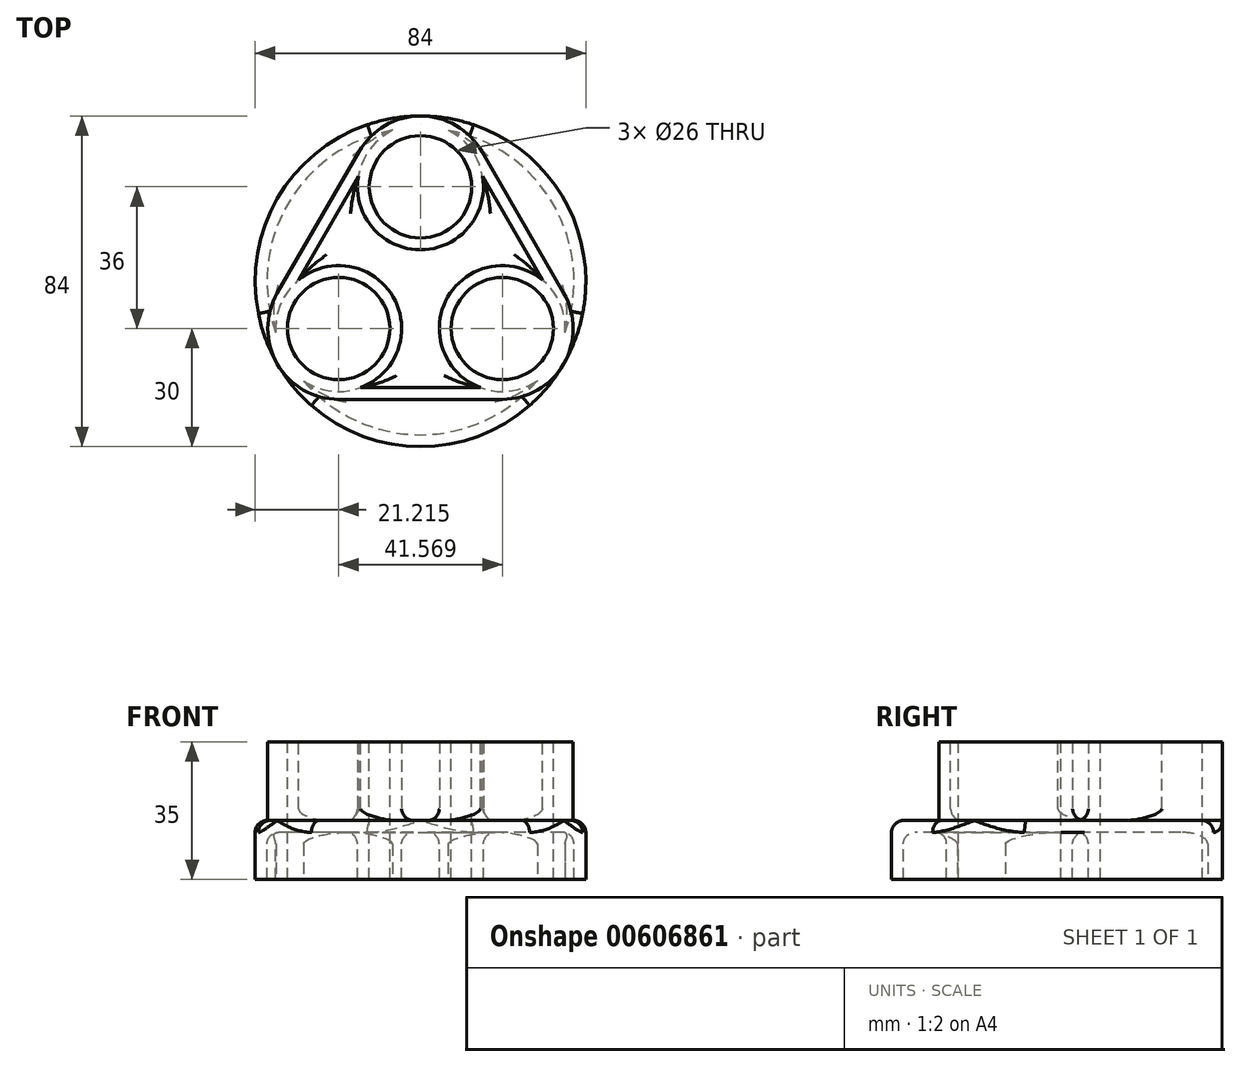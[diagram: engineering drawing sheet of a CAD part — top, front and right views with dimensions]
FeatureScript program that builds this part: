
annotation { "Feature Type Name" : "Feature", "Feature Type Description" : "" }
export const myFeature = defineFeature(function(context is Context, id is Id, definition is map)
    precondition{}
    {
        {
            var Q0;
            Q0=qCreatedBy(makeId("Top.planeOp"),FACE);
            var sketch = newSketch(context, id + "F0", { "sketchPlane" : qUnion([Q0])});
            skCircle(sketch, "E0", {"center": v(0, 24) * mm, "radius": 13 * mm});
            skLineSegment(sketch, "E1", {"start": v(0, 24) * mm, "end": v(0, 0) * mm, "construction": true});
            skCircle(sketch, "E2", {"center": v(-20.78, -12) * mm, "radius": 13 * mm});
            skCircle(sketch, "E3", {"center": v(20.78, -12) * mm, "radius": 13 * mm});
            skLineSegment(sketch, "E4", {"start": v(0, 0) * mm, "end": v(-20.78, -12) * mm, "construction": true});
            skLineSegment(sketch, "E5", {"start": v(0, 0) * mm, "end": v(20.78, -12) * mm, "construction": true});
            skCircle(sketch, "E6", {"center": v(0, 0) * mm, "radius": 42 * mm});
            skCircle(sketch, "E7.0", {"center": v(0, 24) * mm, "radius": 16 * mm});
            skCircle(sketch, "E8.0", {"center": v(-20.78, -12) * mm, "radius": 16 * mm});
            skCircle(sketch, "E9.0", {"center": v(20.78, -12) * mm, "radius": 16 * mm});
            skSolve(sketch);
        }
        {
            var Q0;
            Q0=makeQuery(id+"F0.imprint","IMPRINT",FACE,{"disambiguationData":[TD([[makeQuery(id+"F0.imprint","IMPRINT",EDGE,{"derivedFrom":sQuery(id+"F0.wireOp",EDGE,"E6")}),1.0]])]});
            var Q1;
            Q1=makeQuery(id+"F0.imprint","IMPRINT",FACE,{"disambiguationData":[TD([[makeQuery(id+"F0.imprint","IMPRINT",EDGE,{"derivedFrom":sQuery(id+"F0.wireOp",EDGE,"E3")}),-1.0]])]});
            var Q2;
            Q2=makeQuery(id+"F0.imprint","IMPRINT",FACE,{"disambiguationData":[TD([[makeQuery(id+"F0.imprint","IMPRINT",EDGE,{"derivedFrom":sQuery(id+"F0.wireOp",EDGE,"E0")}),-1.0]])]});
            var Q3;
            Q3=makeQuery(id+"F0.imprint","IMPRINT",FACE,{"disambiguationData":[TD([[makeQuery(id+"F0.imprint","IMPRINT",EDGE,{"derivedFrom":sQuery(id+"F0.wireOp",EDGE,"E2")}),-1.0]])]});
            extrude(context, id + "F1", {"entities" : qUnion([Q0, Q1, Q2, Q3]), "oppositeDirection" : true, "depth" : 15 * mm, "offsetDistance" : 25 * mm});
        }
        {
            var Q0;
            Q0=makeQuery(id+"F0.imprint","IMPRINT",FACE,{"disambiguationData":[TD([[makeQuery(id+"F0.imprint","IMPRINT",EDGE,{"derivedFrom":sQuery(id+"F0.wireOp",EDGE,"E3")}),-1.0]])]});
            var Q1;
            Q1=makeQuery(id+"F0.imprint","IMPRINT",FACE,{"disambiguationData":[TD([[makeQuery(id+"F0.imprint","IMPRINT",EDGE,{"derivedFrom":sQuery(id+"F0.wireOp",EDGE,"E2")}),-1.0]])]});
            var Q2;
            Q2=makeQuery(id+"F0.imprint","IMPRINT",FACE,{"disambiguationData":[TD([[makeQuery(id+"F0.imprint","IMPRINT",EDGE,{"derivedFrom":sQuery(id+"F0.wireOp",EDGE,"E0")}),-1.0]])]});
            extrude(context, id + "F2", {"entities" : qUnion([Q0, Q1, Q2]), "operationType" : NewBodyOperationType.ADD, "depth" : 20 * mm, "offsetDistance" : 25 * mm});
        }
        {
            var Q0;
            Q0=makeQuery(id+"F1.opExtrude","CAP_FACE",FACE,{"disambiguationData":[OSD([sQuery(id+"F0.wireOp",EDGE,"E0"),sQuery(id+"F0.wireOp",EDGE,"E2"),sQuery(id+"F0.wireOp",EDGE,"E3"),sQuery(id+"F0.wireOp",EDGE,"E6")])],"isStart":false});
            shell(context, id + "F3", {"entities" : qUnion([Q0]), "thickness" : 3 * mm});
        }
        {
            var Q0;
            Q0=makeQuery(id+"F2.opExtrude","CAP_FACE",FACE,{"disambiguationData":[OSD([sQuery(id+"F0.wireOp",EDGE,"E0"),sQuery(id+"F0.wireOp",EDGE,"E7.0")])],"isStart":false});
            var sketch = newSketch(context, id + "F4", { "sketchPlane" : qUnion([Q0])});
            skArc(sketch, "E10.0", {"start": v(17.97, 22.88) * mm, "mid": v(0, 42) * mm, "end": v(-17.97, 22.88) * mm});
            skArc(sketch, "E11.0", {"start": v(10.83, -27) * mm, "mid": v(36.37, -21) * mm, "end": v(28.8, 4.12) * mm});
            skCircle(sketch, "E12.0", {"center": v(0, 0) * mm, "radius": 47 * mm});
            skArc(sketch, "E13.0", {"start": v(-28.8, 4.12) * mm, "mid": v(-36.37, -21) * mm, "end": v(-10.83, -27) * mm});
            skLineSegment(sketch, "E14", {"start": v(-36.37, -3) * mm, "end": v(-15.59, 33) * mm});
            skLineSegment(sketch, "E15", {"start": v(15.59, 33) * mm, "end": v(36.37, -3) * mm});
            skLineSegment(sketch, "E16", {"start": v(20.78, -30) * mm, "end": v(-20.78, -30) * mm});
            skLineSegment(sketch, "E17.0", {"start": v(13, 31.49) * mm, "end": v(33.78, -4.51) * mm});
            skLineSegment(sketch, "E18.0", {"start": v(-33.77, -4.49) * mm, "end": v(-12.98, 31.51) * mm});
            skLineSegment(sketch, "E19.0", {"start": v(20.8, -27) * mm, "end": v(-20.77, -27) * mm});
            skCircle(sketch, "E20.0", {"center": v(-20.78, -12) * mm, "radius": 13 * mm});
            skCircle(sketch, "E21.0", {"center": v(20.78, -12) * mm, "radius": 13 * mm});
            skCircle(sketch, "E22.0", {"center": v(0, 24) * mm, "radius": 13 * mm});
            skCircle(sketch, "E23.0.0", {"center": v(20.78, -12) * mm, "radius": 16 * mm});
            skCircle(sketch, "E24.0.0", {"center": v(-20.78, -12) * mm, "radius": 16 * mm});
            skCircle(sketch, "E25.0.0", {"center": v(0, 24) * mm, "radius": 16 * mm});
            skSolve(sketch);
        }
        {
            var Q0;
            {var subQ0=sQuery(id+"F4.wireOp",EDGE,"E10.0");var subQ6=makeQuery(id+"F4.imprint","INTERSECT",VERTEX,{"derivedFrom":[subQ0,sQuery(id+"F4.wireOp",EDGE,"E14")]});Q0=makeQuery(id+"F4.imprint","IMPRINT",FACE,{"disambiguationData":[TD([[makeQuery(id+"F4.imprint","IMPRINT",EDGE,{"disambiguationData":[TD([[subQ6,1.0]])],"derivedFrom":subQ0}),1.0]])]});}
            var Q1;
            {var subQ0=sQuery(id+"F4.wireOp",EDGE,"E15");Q1=makeQuery(id+"F4.imprint","IMPRINT",FACE,{"disambiguationData":[TD([[makeQuery(id+"F4.imprint","IMPRINT",EDGE,{"derivedFrom":subQ0}),-1.0]])]});}
            var Q2;
            Q2=makeQuery(id+"F4.imprint","IMPRINT",FACE,{"disambiguationData":[TD([[makeQuery(id+"F4.imprint","IMPRINT",EDGE,{"derivedFrom":makeQuery(id+"F2.opExtrude","CAP_EDGE",EDGE,{"disambiguationData":[OSD([sQuery(id+"F0.wireOp",EDGE,"E0")])],"isStart":false})}),-1.0]])]});
            var Q3;
            {var subQ0=sQuery(id+"F4.wireOp",EDGE,"E16");Q3=makeQuery(id+"F4.imprint","IMPRINT",FACE,{"disambiguationData":[TD([[makeQuery(id+"F4.imprint","IMPRINT",EDGE,{"derivedFrom":subQ0}),-1.0]])]});}
            var Q4;
            {var subQ0=sQuery(id+"F4.wireOp",EDGE,"E14");Q4=makeQuery(id+"F4.imprint","IMPRINT",FACE,{"disambiguationData":[TD([[makeQuery(id+"F4.imprint","IMPRINT",EDGE,{"derivedFrom":subQ0}),-1.0]])]});}
            var Q5;
            {var subQ0=sQuery(id+"F4.wireOp",EDGE,"E18.0");var subQ1=sQuery(id+"F4.wireOp",EDGE,"E13.0");var subQ2=makeQuery(id+"F4.imprint","INTERSECT",VERTEX,{"derivedFrom":[subQ1,subQ0]});Q5=makeQuery(id+"F4.imprint","IMPRINT",FACE,{"disambiguationData":[TD([[makeQuery(id+"F4.imprint","IMPRINT",EDGE,{"disambiguationData":[TD([[subQ2,-1.0]])],"derivedFrom":subQ1}),1.0]])]});}
            var Q6;
            {var subQ1=sQuery(id+"F4.wireOp",EDGE,"E11.0");var subQ7=sQuery(id+"F4.wireOp",EDGE,"E19.0");var subQ9=makeQuery(id+"F4.imprint","INTERSECT",VERTEX,{"derivedFrom":[subQ1,subQ7]});Q6=makeQuery(id+"F4.imprint","IMPRINT",FACE,{"disambiguationData":[TD([[makeQuery(id+"F4.imprint","IMPRINT",EDGE,{"disambiguationData":[TD([[subQ9,-1.0]])],"derivedFrom":subQ1}),1.0]])]});}
            var Q7;
            Q7=makeQuery(id+"F4.imprint","IMPRINT",FACE,{"disambiguationData":[TD([[makeQuery(id+"F4.imprint","IMPRINT",EDGE,{"derivedFrom":sQuery(id+"F4.wireOp",EDGE,"E21.0")}),-1.0]])]});
            var Q8;
            Q8=makeQuery(id+"F4.imprint","IMPRINT",FACE,{"disambiguationData":[TD([[makeQuery(id+"F4.imprint","IMPRINT",EDGE,{"derivedFrom":sQuery(id+"F4.wireOp",EDGE,"E20.0")}),-1.0]])]});
            var Q9;
            Q9=makeQuery(id+"F4.imprint","IMPRINT",FACE,{"disambiguationData":[TD([[makeQuery(id+"F4.imprint","IMPRINT",EDGE,{"derivedFrom":sQuery(id+"F4.wireOp",EDGE,"E22.0")}),-1.0]])]});
            var Q10;
            Q10=makeQuery(id+"F1.opExtrude","CAP_FACE",FACE,{"disambiguationData":[OSD([sQuery(id+"F0.wireOp",EDGE,"E0"),sQuery(id+"F0.wireOp",EDGE,"E2"),sQuery(id+"F0.wireOp",EDGE,"E3"),sQuery(id+"F0.wireOp",EDGE,"E6")])],"isStart":true});
            extrude(context, id + "F5", {"entities" : qUnion([Q0, Q1, Q2, Q3, Q4, Q5, Q6, Q7, Q8, Q9]), "operationType" : NewBodyOperationType.ADD, "endBound" : BoundingType.UP_TO_SURFACE, "oppositeDirection" : true, "depth" : 20 * mm, "endBoundEntityFace" : qUnion([Q10]), "offsetDistance" : 25 * mm});
        }
        {
            var Q0;
            {var subQ0=sQuery(id+"F0.wireOp",EDGE,"E6");Q0=makeQuery(id+"F5.boolean.opBoolean","SPLIT",EDGE,{"disambiguationData":[TD([makeQuery(id+"F1.opExtrude","CAP_FACE",FACE,{"disambiguationData":[OSD([sQuery(id+"F0.wireOp",EDGE,"E0"),sQuery(id+"F0.wireOp",EDGE,"E2"),sQuery(id+"F0.wireOp",EDGE,"E3"),subQ0])],"isStart":true}),makeQuery(id+"F1.opExtrude","SWEPT_FACE",FACE,{"disambiguationData":[OSD([subQ0])]}),makeQuery(id+"F5.opExtrude","SWEPT_FACE",FACE,{"disambiguationData":[OSD([sQuery(id+"F4.wireOp",EDGE,"E11.0")])]}),makeQuery(id+"F5.opExtrude","SWEPT_FACE",FACE,{"disambiguationData":[OSD([sQuery(id+"F4.wireOp",EDGE,"E13.0")])]})])],"derivedFrom":makeQuery(id+"F1.opExtrude","CAP_EDGE",EDGE,{"disambiguationData":[OSD([subQ0])],"isStart":true})});}
            fillet(context, id + "F6", {"entities" : qUnion([Q0]), "radius" : 3 * mm, "tangentPropagation" : true, "allowEdgeOverflow" : false});
        }
        {
            var Q0;
            Q0=makeQuery(id+"F5.opExtrude","TWEAK_EDGE",EDGE,{"derivedFrom":[makeQuery(id+"F1.opExtrude","CAP_FACE",FACE,{"disambiguationData":[OSD([sQuery(id+"F0.wireOp",EDGE,"E0"),sQuery(id+"F0.wireOp",EDGE,"E2"),sQuery(id+"F0.wireOp",EDGE,"E3"),sQuery(id+"F0.wireOp",EDGE,"E6")])],"isStart":true}),makeQuery(id+"F4.imprint","IMPRINT",EDGE,{"derivedFrom":sQuery(id+"F4.wireOp",EDGE,"E16")})]});
            var Q1;
            Q1=makeQuery(id+"F5.opExtrude","TWEAK_EDGE",EDGE,{"derivedFrom":[makeQuery(id+"F1.opExtrude","CAP_FACE",FACE,{"disambiguationData":[OSD([sQuery(id+"F0.wireOp",EDGE,"E0"),sQuery(id+"F0.wireOp",EDGE,"E2"),sQuery(id+"F0.wireOp",EDGE,"E3"),sQuery(id+"F0.wireOp",EDGE,"E6")])],"isStart":true}),makeQuery(id+"F4.imprint","IMPRINT",EDGE,{"derivedFrom":sQuery(id+"F4.wireOp",EDGE,"E15")})]});
            var Q2;
            Q2=makeQuery(id+"F5.opExtrude","TWEAK_EDGE",EDGE,{"derivedFrom":[makeQuery(id+"F1.opExtrude","CAP_FACE",FACE,{"disambiguationData":[OSD([sQuery(id+"F0.wireOp",EDGE,"E0"),sQuery(id+"F0.wireOp",EDGE,"E2"),sQuery(id+"F0.wireOp",EDGE,"E3"),sQuery(id+"F0.wireOp",EDGE,"E6")])],"isStart":true}),makeQuery(id+"F4.imprint","IMPRINT",EDGE,{"derivedFrom":sQuery(id+"F4.wireOp",EDGE,"E14")})]});
            var Q3;
            Q3=makeQuery(id+"F5.boolean.opBoolean","SPLIT",FACE,{"disambiguationData":[TD([makeQuery(id+"F2.opExtrude","SWEPT_FACE",FACE,{"disambiguationData":[OSD([sQuery(id+"F0.wireOp",EDGE,"E7.0")])]})])],"derivedFrom":makeQuery(id+"F1.opExtrude","CAP_FACE",FACE,{"disambiguationData":[OSD([sQuery(id+"F0.wireOp",EDGE,"E0"),sQuery(id+"F0.wireOp",EDGE,"E2"),sQuery(id+"F0.wireOp",EDGE,"E3"),sQuery(id+"F0.wireOp",EDGE,"E6")])],"isStart":true})});
            var Q4;
            Q4=makeQuery(id+"F3.opShell","OFFSET_FACE",FACE,{"disambiguationData":[OSD([sQuery(id+"F0.wireOp",EDGE,"E0"),sQuery(id+"F0.wireOp",EDGE,"E2"),sQuery(id+"F0.wireOp",EDGE,"E3"),sQuery(id+"F0.wireOp",EDGE,"E6")])]});
            fillet(context, id + "F7", {"entities" : qUnion([Q0, Q1, Q2, Q3, Q4]), "radius" : 3 * mm, "tangentPropagation" : true, "allowEdgeOverflow" : false});
        }
    });
